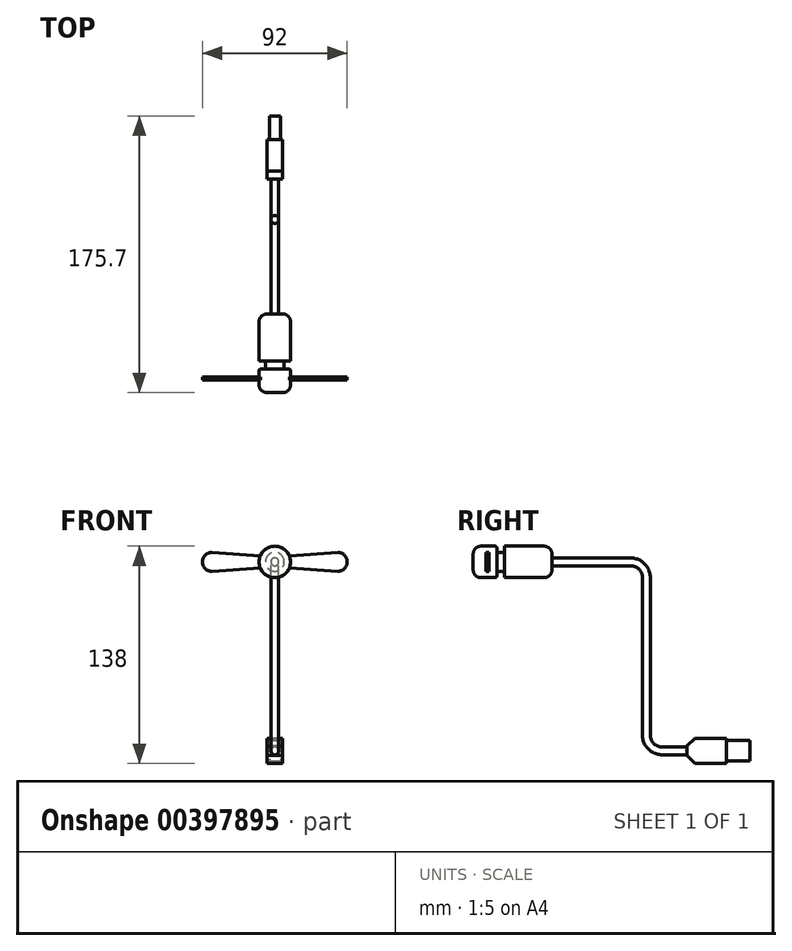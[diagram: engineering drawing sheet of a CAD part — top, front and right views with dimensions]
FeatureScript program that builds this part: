
annotation { "Feature Type Name" : "Feature", "Feature Type Description" : "" }
export const myFeature = defineFeature(function(context is Context, id is Id, definition is map)
    precondition{}
    {
        {
            var Q0;
            Q0=qCreatedBy(makeId("Right.planeOp"),FACE);
            var sketch = newSketch(context, id + "F0", { "sketchPlane" : qUnion([Q0])});
            skLineSegment(sketch, "E0.bottom", {"start": v(20, 8) * mm, "end": v(-20, 8) * mm});
            skLineSegment(sketch, "E0.top", {"start": v(20, -8) * mm, "end": v(-20, -8) * mm});
            skLineSegment(sketch, "E0.left", {"start": v(20, 8) * mm, "end": v(20, -8) * mm});
            skLineSegment(sketch, "E0.right", {"start": v(-20, 8) * mm, "end": v(-20, -8) * mm});
            skPoint(sketch, "E0.middle", {"position": v(0, 0) * mm});
            skSolve(sketch);
        }
        {
            var Q0;
            Q0 = qSketchRegion(id + "F0", true);
            extrude(context, id + "F1", {"entities" : qUnion([Q0]), "depth" : 10 * mm});
        }
        {
            var Q0;
            Q0=makeQuery(id+"F1.opExtrude","CAP_FACE",FACE,{"disambiguationData":[OSD([sQuery(id+"F0.wireOp",EDGE,"E0.bottom"),sQuery(id+"F0.wireOp",EDGE,"E0.top"),sQuery(id+"F0.wireOp",EDGE,"E0.left"),sQuery(id+"F0.wireOp",EDGE,"E0.right")])],"isStart":false});
            var Q1;
            Q1=makeQuery(id+"F1.opExtrude","CAP_FACE",FACE,{"disambiguationData":[OSD([sQuery(id+"F0.wireOp",EDGE,"E0.bottom"),sQuery(id+"F0.wireOp",EDGE,"E0.top"),sQuery(id+"F0.wireOp",EDGE,"E0.left"),sQuery(id+"F0.wireOp",EDGE,"E0.right")])],"isStart":true});
            cPlane(context, id + "F2", {"entities" : qUnion([Q0, Q1]), "cplaneType" : CPlaneType.MID_PLANE, "offset" : 25 * mm, "width" : 150 * mm, "height" : 150 * mm});
        }
        {
            var Q0;
            Q0=makeQuery(id+"F1.opExtrude","SWEPT_FACE",FACE,{"disambiguationData":[OSD([sQuery(id+"F0.wireOp",EDGE,"E0.right")])]});
            var sketch = newSketch(context, id + "F3", { "sketchPlane" : qUnion([Q0])});
            skCircle(sketch, "E1", {"center": v(5, 0) * mm, "radius": 2.5 * mm});
            skSolve(sketch);
        }
        {
            var Q0;
            Q0=qCreatedBy(id+"F2.planeOp",FACE);
            var sketch = newSketch(context, id + "F4", { "sketchPlane" : qUnion([Q0])});
            skLineSegment(sketch, "E2", {"start": v(-20, 0) * mm, "end": v(-35.7, 0) * mm});
            skLineSegment(sketch, "E3", {"start": v(-45.7, 10) * mm, "end": v(-45.7, 110) * mm});
            skLineSegment(sketch, "E4", {"start": v(-55.7, 120) * mm, "end": v(-155.7, 120) * mm});
            skPoint(sketch, "E5.visualSharp", {"position": v(-45.7, 0) * mm});
            skArc(sketch, "E5.filletArc", {"start": v(-45.7, 10) * mm, "mid": v(-42.77, 2.93) * mm, "end": v(-35.7, 0) * mm});
            skPoint(sketch, "E6.visualSharp", {"position": v(-45.7, 120) * mm});
            skArc(sketch, "E6.filletArc", {"start": v(-45.7, 110) * mm, "mid": v(-48.63, 117.07) * mm, "end": v(-55.7, 120) * mm});
            skSolve(sketch);
        }
        {
            var Q0;
            Q0 = qSketchRegion(id + "F3", true);
            var Q1;
            Q1 = qConstructionFilter(qBodyType(qCreatedBy(id + "F4" ,EDGE), BodyType.WIRE), ConstructionObject.NO);
            sweep(context, id + "F5", {"operationType" : NewBodyOperationType.ADD, "profiles" : qUnion([Q0]), "path" : qUnion([Q1])});
        }
        {
            var Q0;
            Q0=makeQuery(id+"F5.opSweep","CAP_FACE",FACE,{"disambiguationData":[OSD([sQuery(id+"F3.wireOp",EDGE,"E1"),sQuery(id+"F4.wireOp",VERTEX,"E4.end")])],"isStart":false});
            var sketch = newSketch(context, id + "F6", { "sketchPlane" : qUnion([Q0])});
            skCircle(sketch, "E7", {"center": v(5, 120) * mm, "radius": 10 * mm});
            skSolve(sketch);
        }
        {
            var Q0;
            Q0=makeQuery(id+"F6.imprint","IMPRINT",FACE,{"disambiguationData":[TD([[makeQuery(id+"F6.imprint","IMPRINT",EDGE,{"derivedFrom":sQuery(id+"F6.wireOp",EDGE,"E7")}),1.0]])]});
            extrude(context, id + "F7", {"entities" : qUnion([Q0]), "operationType" : NewBodyOperationType.ADD, "oppositeDirection" : true, "depth" : 50 * mm});
        }
        {
            var Q0;
            Q0=makeQuery(id+"F7.opExtrude","CAP_EDGE",EDGE,{"disambiguationData":[OSD([sQuery(id+"F6.wireOp",EDGE,"E7")])],"isStart":false});
            var Q1;
            Q1=makeQuery(id+"F7.opExtrude","CAP_EDGE",EDGE,{"disambiguationData":[OSD([sQuery(id+"F6.wireOp",EDGE,"E7")])],"isStart":true});
            fillet(context, id + "F8", {"entities" : qUnion([Q0, Q1]), "radius" : 5 * mm, "tangentPropagation" : true, "allowEdgeOverflow" : false});
        }
        {
            var Q0;
            Q0=makeQuery(id+"F1.opExtrude","SWEPT_EDGE",EDGE,{"disambiguationData":[OSD([sQuery(id+"F0.wireOp",EDGE,"E0.bottom"),sQuery(id+"F0.wireOp",EDGE,"E0.right")])]});
            var Q1;
            Q1=makeQuery(id+"F1.opExtrude","SWEPT_EDGE",EDGE,{"disambiguationData":[OSD([sQuery(id+"F0.wireOp",EDGE,"E0.top"),sQuery(id+"F0.wireOp",EDGE,"E0.right")])]});
            chamfer(context, id + "F9", {"entities" : qUnion([Q0, Q1]), "width" : 5 * mm, "tangentPropagation" : true});
        }
        {
            var Q0;
            Q0=makeQuery(id+"F1.opExtrude","SWEPT_FACE",FACE,{"disambiguationData":[OSD([sQuery(id+"F0.wireOp",EDGE,"E0.left")])]});
            var sketch = newSketch(context, id + "F10", { "sketchPlane" : qUnion([Q0])});
            skLineSegment(sketch, "E8.bottom", {"start": v(-1.5, 6.5) * mm, "end": v(-8.5, 6.5) * mm});
            skLineSegment(sketch, "E8.top", {"start": v(-1.5, -6.5) * mm, "end": v(-8.5, -6.5) * mm});
            skLineSegment(sketch, "E8.left", {"start": v(-1.5, 6.5) * mm, "end": v(-1.5, -6.5) * mm});
            skLineSegment(sketch, "E8.right", {"start": v(-8.5, 6.5) * mm, "end": v(-8.5, -6.5) * mm});
            skPoint(sketch, "E8.middle", {"position": v(-5, 0) * mm});
            skPoint(sketch, "E8.middle.positionSnap0", {"position": v(-5, 8) * mm});
            skPoint(sketch, "E8.middle.positionSnap1", {"position": v(-10, 0) * mm});
            skPoint(sketch, "E8.centerSnap0", {"position": v(-5, 8) * mm});
            skPoint(sketch, "E8.centerSnap1", {"position": v(-10, 0) * mm});
            skLineSegment(sketch, "E9.0.0", {"start": v(0, -8) * mm, "end": v(0, 8) * mm});
            skLineSegment(sketch, "E9.0.1", {"start": v(0, 8) * mm, "end": v(-10, 8) * mm});
            skLineSegment(sketch, "E9.0.2", {"start": v(-10, 8) * mm, "end": v(-10, -8) * mm});
            skLineSegment(sketch, "E9.0.3", {"start": v(-10, -8) * mm, "end": v(0, -8) * mm});
            skSolve(sketch);
        }
        {
            var Q0;
            Q0 = qSketchRegion(id + "F10", true);
            extrude(context, id + "F11", {"entities" : qUnion([Q0]), "operationType" : NewBodyOperationType.REMOVE, "oppositeDirection" : true, "depth" : 15 * mm});
        }
        {
            var Q0;
            Q0=makeQuery(id+"F7.opExtrude","CAP_FACE",FACE,{"disambiguationData":[OSD([sQuery(id+"F3.wireOp",EDGE,"E1"),sQuery(id+"F4.wireOp",VERTEX,"E4.end"),sQuery(id+"F6.wireOp",EDGE,"E7")])],"isStart":false});
            cPlane(context, id + "F12", {"entities" : qUnion([Q0]), "cplaneType" : CPlaneType.OFFSET, "offset" : 30 * mm, "oppositeDirection" : true, "width" : 150 * mm, "height" : 150 * mm});
        }
        {
            var Q0;
            Q0=qCreatedBy(id+"F12.planeOp",FACE);
            var sketch = newSketch(context, id + "F13", { "sketchPlane" : qUnion([Q0])});
            skCircle(sketch, "E10.0", {"center": v(-5, 120) * mm, "radius": 10 * mm});
            skCircle(sketch, "E11.0", {"center": v(-5, 120) * mm, "radius": 6 * mm});
            skSolve(sketch);
        }
        {
            var Q0;
            Q0 = qSketchRegion(id + "F13", true);
            extrude(context, id + "F14", {"entities" : qUnion([Q0]), "operationType" : NewBodyOperationType.REMOVE, "oppositeDirection" : true, "depth" : 5 * mm});
        }
        {
            var Q0;
            Q0=makeQuery(id+"F14.boolean.opBoolean","COPY",EDGE,{"derivedFrom":makeQuery(id+"F14.opExtrude","CAP_EDGE",EDGE,{"disambiguationData":[OSD([sQuery(id+"F13.wireOp",EDGE,"E10.0")])],"isStart":true})});
            var Q1;
            Q1=makeQuery(id+"F14.boolean.opBoolean","COPY",EDGE,{"derivedFrom":makeQuery(id+"F14.opExtrude","CAP_EDGE",EDGE,{"disambiguationData":[OSD([sQuery(id+"F13.wireOp",EDGE,"E10.0")])],"isStart":false})});
            fillet(context, id + "F15", {"entities" : qUnion([Q0, Q1]), "radius" : 1 * mm, "tangentPropagation" : true, "allowEdgeOverflow" : false});
        }
        {
            var Q0;
            Q0=qCreatedBy(id+"F12.planeOp",FACE);
            cPlane(context, id + "F16", {"entities" : qUnion([Q0]), "cplaneType" : CPlaneType.OFFSET, "offset" : 10 * mm, "oppositeDirection" : true, "width" : 150 * mm, "height" : 150 * mm});
        }
        {
            var Q0;
            Q0=qCreatedBy(id+"F16.planeOp",FACE);
            var sketch = newSketch(context, id + "F17", { "sketchPlane" : qUnion([Q0])});
            skArc(sketch, "E12.0", {"start": v(-0.16, 116.46) * mm, "mid": v(1, 120) * mm, "end": v(-0.16, 123.54) * mm});
            skLineSegment(sketch, "E13", {"start": v(-0.16, 123.54) * mm, "end": v(35, 126) * mm});
            skLineSegment(sketch, "E14", {"start": v(-5, 120) * mm, "end": v(28.46, 120) * mm, "construction": true});
            skLineSegment(sketch, "E15", {"start": v(-5, 120) * mm, "end": v(-5, 134.59) * mm, "construction": true});
            skLineSegment(sketch, "E16.MirrorCS", {"start": v(-0.16, 116.46) * mm, "end": v(35, 114) * mm});
            skArc(sketch, "E17", {"start": v(35, 114) * mm, "mid": v(41, 120) * mm, "end": v(35, 126) * mm});
            skArc(sketch, "E18.MirrorCS", {"start": v(-9.84, 116.46) * mm, "mid": v(-11, 120) * mm, "end": v(-9.84, 123.54) * mm});
            skLineSegment(sketch, "E19.MirrorCS", {"start": v(-9.84, 116.46) * mm, "end": v(-45, 114) * mm});
            skLineSegment(sketch, "E20.MirrorCS", {"start": v(-9.84, 123.54) * mm, "end": v(-45, 126) * mm});
            skArc(sketch, "E21.MirrorCS", {"start": v(-45, 114) * mm, "mid": v(-51, 120) * mm, "end": v(-45, 126) * mm});
            skSolve(sketch);
        }
        {
            var Q0;
            Q0 = qSketchRegion(id + "F17", true);
            extrude(context, id + "F18", {"entities" : qUnion([Q0]), "operationType" : NewBodyOperationType.ADD, "oppositeDirection" : true, "depth" : 2 * mm});
        }
    });
